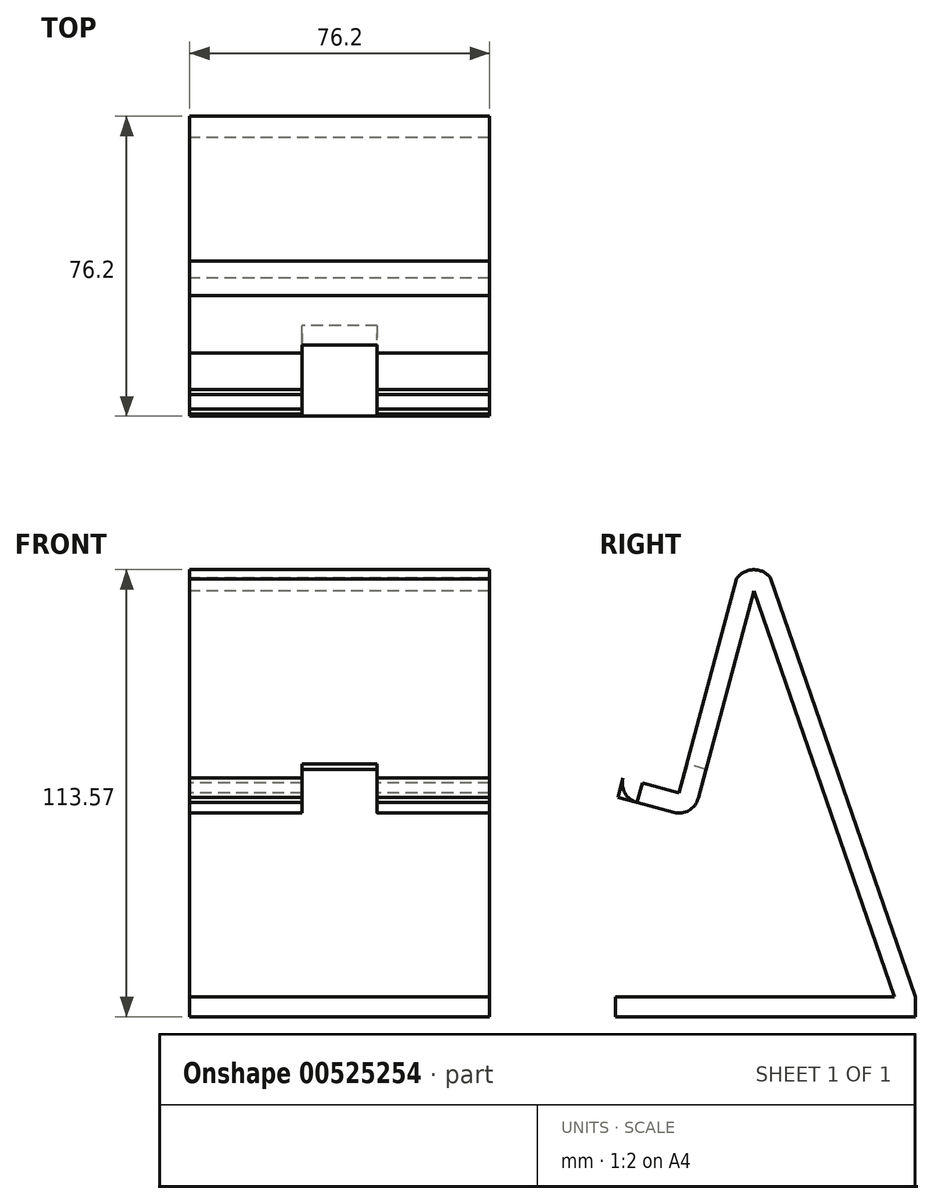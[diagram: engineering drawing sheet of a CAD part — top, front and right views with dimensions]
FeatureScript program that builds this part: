
annotation { "Feature Type Name" : "Feature", "Feature Type Description" : "" }
export const myFeature = defineFeature(function(context is Context, id is Id, definition is map)
    precondition{}
    {
        {
            var Q0;
            Q0=qCreatedBy(makeId("Right.planeOp"),FACE);
            var sketch = newSketch(context, id + "F0", { "sketchPlane" : qUnion([Q0])});
            skLineSegment(sketch, "E0", {"start": v(-24.63, 0) * mm, "end": v(51.57, 0) * mm});
            skLineSegment(sketch, "E1", {"start": v(51.57, 0) * mm, "end": v(51.57, -5.08) * mm});
            skLineSegment(sketch, "E2", {"start": v(51.57, -5.08) * mm, "end": v(-24.63, -5.08) * mm});
            skLineSegment(sketch, "E3", {"start": v(-24.63, -5.08) * mm, "end": v(-24.63, 0) * mm});
            skLineSegment(sketch, "E4", {"start": v(-9.86, 46.84) * mm, "end": v(9.86, 120.45) * mm});
            skLineSegment(sketch, "E5", {"start": v(-9.86, 46.84) * mm, "end": v(-9.86, 70.9) * mm});
            skLineSegment(sketch, "E6", {"start": v(9.86, 120.45) * mm, "end": v(51.57, 0) * mm});
            skLineSegment(sketch, "E7", {"start": v(7.51, 111.7) * mm, "end": v(46.2, 0) * mm});
            skLineSegment(sketch, "E8", {"start": v(22.61, 68.1) * mm, "end": v(27.41, 69.76) * mm});
            skLineSegment(sketch, "E9", {"start": v(10.48, 103.13) * mm, "end": v(-4.98, 45.45) * mm});
            skLineSegment(sketch, "E10", {"start": v(-4.98, 45.45) * mm, "end": v(-9.86, 46.84) * mm});
            skLineSegment(sketch, "E11", {"start": v(1.85, 90.54) * mm, "end": v(6.75, 89.23) * mm});
            skLineSegment(sketch, "E12", {"start": v(-9.86, 46.84) * mm, "end": v(-19.19, 49.34) * mm});
            skLineSegment(sketch, "E13", {"start": v(-19.19, 49.34) * mm, "end": v(-16.88, 57.93) * mm});
            skLineSegment(sketch, "E14", {"start": v(-17.87, 54.25) * mm, "end": v(-8.55, 51.75) * mm});
            skLineSegment(sketch, "E15", {"start": v(-16.88, 57.93) * mm, "end": v(-21.8, 59.24) * mm});
            skLineSegment(sketch, "E16", {"start": v(-21.8, 59.24) * mm, "end": v(-24.1, 50.65) * mm});
            skLineSegment(sketch, "E17", {"start": v(-24.1, 50.65) * mm, "end": v(-19.19, 49.34) * mm});
            skLineSegment(sketch, "E18", {"start": v(-24.63, 0) * mm, "end": v(-24.63, 69.94) * mm});
            skArc(sketch, "E19", {"start": v(14.72, 106.4) * mm, "mid": v(10.29, 108.49) * mm, "end": v(6.01, 106.1) * mm});
            skArc(sketch, "E20", {"start": v(-9.86, 46.84) * mm, "mid": v(-6, 47.35) * mm, "end": v(-3.64, 50.43) * mm});
            skArc(sketch, "E21", {"start": v(-19.19, 49.34) * mm, "mid": v(-22.27, 51.7) * mm, "end": v(-22.78, 55.56) * mm});
            skArc(sketch, "E22", {"start": v(-16.88, 57.93) * mm, "mid": v(-20.22, 57.73) * mm, "end": v(-22.78, 55.56) * mm});
            skSolve(sketch);
        }
        {
            var Q0;
            {var subQ0=sQuery(id+"F0.wireOp",EDGE,"E1");Q0=makeQuery(id+"F0.imprint","IMPRINT",FACE,{"disambiguationData":[TD([[makeQuery(id+"F0.imprint","IMPRINT",EDGE,{"derivedFrom":subQ0}),-1.0]])]});}
            var Q1;
            {var subQ5=sQuery(id+"F0.wireOp",EDGE,"E8");Q1=makeQuery(id+"F0.imprint","IMPRINT",FACE,{"disambiguationData":[TD([[makeQuery(id+"F0.imprint","IMPRINT",EDGE,{"derivedFrom":subQ5}),-1.0]])]});}
            var Q2;
            {var subQ1=sQuery(id+"F0.wireOp",EDGE,"E4");var subQ3=sQuery(id+"F0.wireOp",EDGE,"E14");var subQ4=makeQuery(id+"F0.imprint","INTERSECT",VERTEX,{"derivedFrom":[subQ1,subQ3]});Q2=makeQuery(id+"F0.imprint","IMPRINT",FACE,{"disambiguationData":[TD([[makeQuery(id+"F0.imprint","IMPRINT",EDGE,{"disambiguationData":[TD([[subQ4,1.0]])],"derivedFrom":subQ3}),-1.0]])]});}
            var Q3;
            {var subQ0=sQuery(id+"F0.wireOp",EDGE,"E12");Q3=makeQuery(id+"F0.imprint","IMPRINT",FACE,{"disambiguationData":[TD([[makeQuery(id+"F0.imprint","IMPRINT",EDGE,{"derivedFrom":subQ0}),-1.0]])]});}
            var Q4;
            {var subQ0=sQuery(id+"F0.wireOp",EDGE,"E11");Q4=makeQuery(id+"F0.imprint","IMPRINT",FACE,{"disambiguationData":[TD([[makeQuery(id+"F0.imprint","IMPRINT",EDGE,{"derivedFrom":subQ0}),-1.0]])]});}
            var Q5;
            {var subQ0=sQuery(id+"F0.wireOp",EDGE,"E8");Q5=makeQuery(id+"F0.imprint","IMPRINT",FACE,{"disambiguationData":[TD([[makeQuery(id+"F0.imprint","IMPRINT",EDGE,{"derivedFrom":subQ0}),1.0]])]});}
            var Q6;
            {var subQ0=sQuery(id+"F0.wireOp",EDGE,"E21");Q6=makeQuery(id+"F0.imprint","IMPRINT",FACE,{"disambiguationData":[TD([[makeQuery(id+"F0.imprint","IMPRINT",EDGE,{"derivedFrom":subQ0}),-1.0]])]});}
            var Q7;
            {var subQ0=sQuery(id+"F0.wireOp",EDGE,"E11");Q7=makeQuery(id+"F0.imprint","IMPRINT",FACE,{"disambiguationData":[TD([[makeQuery(id+"F0.imprint","IMPRINT",EDGE,{"derivedFrom":subQ0}),1.0]])]});}
            extrude(context, id + "F1", {"entities" : qUnion([Q0, Q1, Q2, Q3, Q4, Q5, Q6, Q7]), "depth" : 76.2 * mm, "offsetDistance" : 25.4 * mm});
        }
        {
            var Q0;
            Q0=makeQuery(id+"F1.opExtrude","SWEPT_FACE",FACE,{"disambiguationData":[OSD([sQuery(id+"F0.wireOp",EDGE,"E12")])]});
            var sketch = newSketch(context, id + "F2", { "sketchPlane" : qUnion([Q0])});
            skLineSegment(sketch, "E23", {"start": v(0, 31.3) * mm, "end": v(28.58, 31.3) * mm});
            skLineSegment(sketch, "E24", {"start": v(28.58, 31.3) * mm, "end": v(28.58, 21.65) * mm});
            skLineSegment(sketch, "E25", {"start": v(28.58, 21.65) * mm, "end": v(47.63, 21.65) * mm});
            skLineSegment(sketch, "E26", {"start": v(47.63, 21.65) * mm, "end": v(47.63, 31.3) * mm});
            skLineSegment(sketch, "E27", {"start": v(47.63, 31.3) * mm, "end": v(28.58, 31.3) * mm});
            skLineSegment(sketch, "E28", {"start": v(47.63, 31.3) * mm, "end": v(47.63, 37.85) * mm});
            skLineSegment(sketch, "E29", {"start": v(47.63, 37.85) * mm, "end": v(28.58, 37.85) * mm});
            skLineSegment(sketch, "E30", {"start": v(28.58, 37.85) * mm, "end": v(28.57, 31.3) * mm});
            skLineSegment(sketch, "E31", {"start": v(28.58, 21.65) * mm, "end": v(28.58, 16.3) * mm});
            skLineSegment(sketch, "E32", {"start": v(28.58, 16.3) * mm, "end": v(47.63, 16.3) * mm});
            skLineSegment(sketch, "E33", {"start": v(47.62, 16.3) * mm, "end": v(47.62, 21.65) * mm});
            skSolve(sketch);
        }
        {
            var Q0;
            Q0 = qSketchRegion(id + "F2", true);
            extrude(context, id + "F3", {"entities" : qUnion([Q0]), "operationType" : NewBodyOperationType.REMOVE, "oppositeDirection" : true, "depth" : 12.7 * mm, "offsetDistance" : 25.4 * mm});
        }
    });
